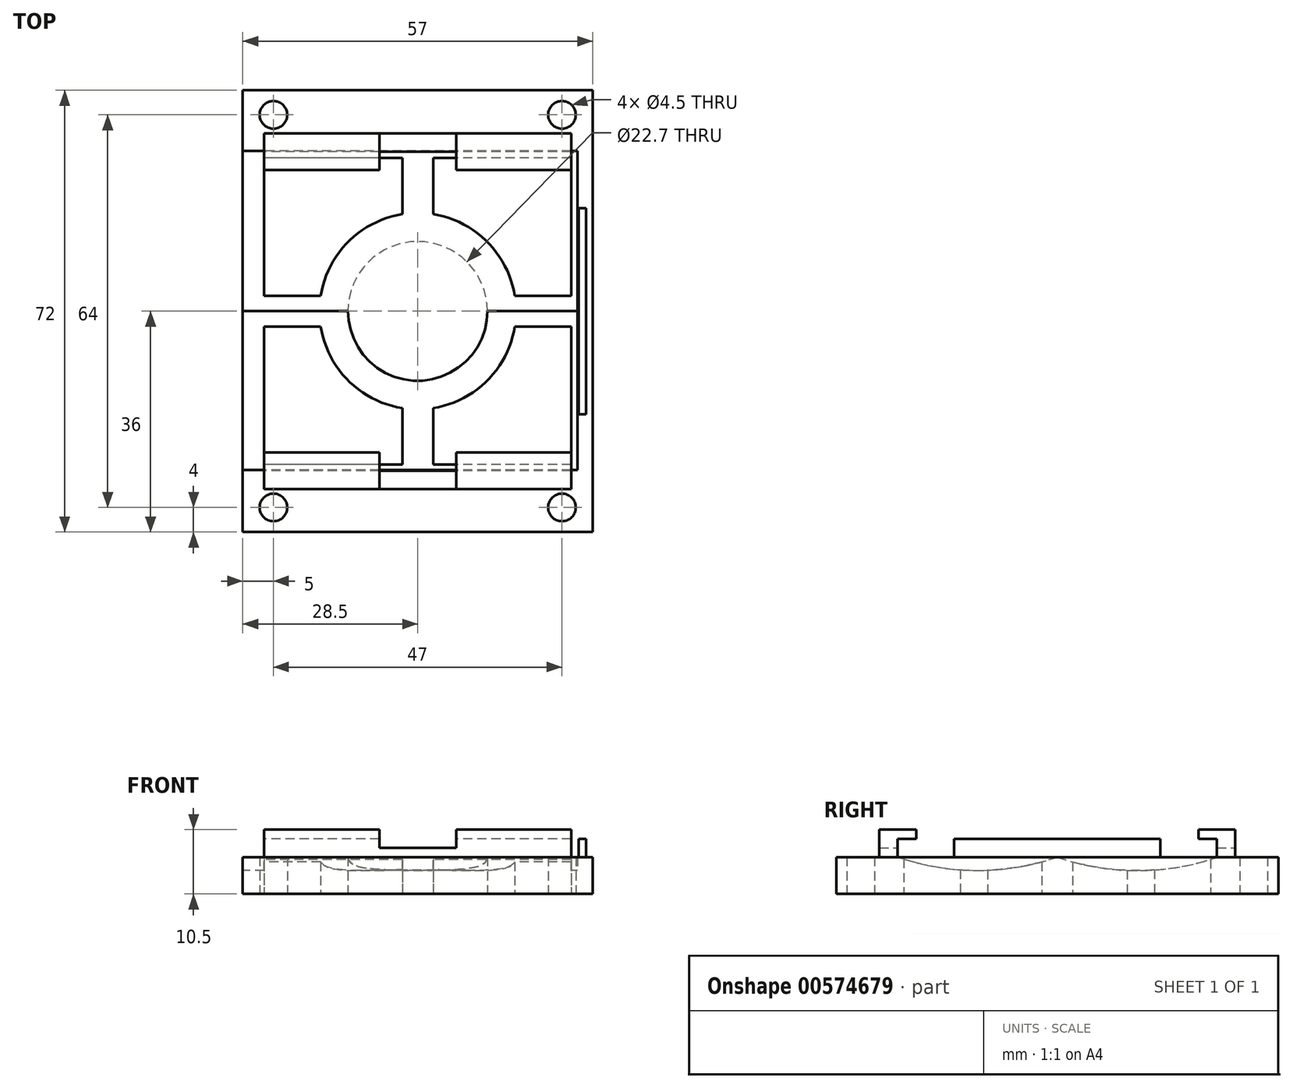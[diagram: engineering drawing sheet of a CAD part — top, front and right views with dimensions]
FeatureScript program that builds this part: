
annotation { "Feature Type Name" : "Feature", "Feature Type Description" : "" }
export const myFeature = defineFeature(function(context is Context, id is Id, definition is map)
    precondition{}
    {
        {
            var Q0;
            Q0=qCreatedBy(makeId("Top.planeOp"),FACE);
            var sketch = newSketch(context, id + "F0", { "sketchPlane" : qUnion([Q0])});
            skLineSegment(sketch, "E0.bottom", {"start": v(25, 25) * mm, "end": v(2.5, 25) * mm});
            skLineSegment(sketch, "E0.top", {"start": v(25, -25) * mm, "end": v(2.5, -25) * mm});
            skLineSegment(sketch, "E0.left", {"start": v(25, 25) * mm, "end": v(25, -25) * mm});
            skLineSegment(sketch, "E0.right", {"start": v(-25, 25) * mm, "end": v(-25, 2.5) * mm});
            skPoint(sketch, "E0.middle", {"position": v(0, 0) * mm});
            skLineSegment(sketch, "E1.bottom", {"start": v(28.5, 36) * mm, "end": v(-28.5, 36) * mm});
            skLineSegment(sketch, "E1.top", {"start": v(28.5, -36) * mm, "end": v(-28.5, -36) * mm});
            skLineSegment(sketch, "E1.left", {"start": v(28.5, 36) * mm, "end": v(28.5, -36) * mm});
            skLineSegment(sketch, "E1.right", {"start": v(-28.5, 36) * mm, "end": v(-28.5, -36) * mm});
            skCircle(sketch, "E2", {"center": v(0, 0) * mm, "radius": 11.35 * mm});
            skArc(sketch, "E3", {"start": v(2.5, -15.8) * mm, "mid": v(11.31, -11.31) * mm, "end": v(15.8, -2.5) * mm});
            skCircle(sketch, "E4", {"center": v(-23.5, 32) * mm, "radius": 2.25 * mm});
            skCircle(sketch, "E5", {"center": v(23.5, 32) * mm, "radius": 2.25 * mm});
            skCircle(sketch, "E6", {"center": v(23.5, -32) * mm, "radius": 2.25 * mm});
            skCircle(sketch, "E7", {"center": v(-23.5, -32) * mm, "radius": 2.25 * mm});
            skLineSegment(sketch, "E8.left", {"start": v(2.5, 25) * mm, "end": v(2.5, 15.8) * mm});
            skLineSegment(sketch, "E8.right", {"start": v(-2.5, 25) * mm, "end": v(-2.5, 15.8) * mm});
            skLineSegment(sketch, "E9.bottom", {"start": v(25, 2.5) * mm, "end": v(15.8, 2.5) * mm});
            skLineSegment(sketch, "E9.top", {"start": v(25, -2.5) * mm, "end": v(15.8, -2.5) * mm});
            skLineSegment(sketch, "E9.left", {"start": v(25, 2.5) * mm, "end": v(25, -2.5) * mm});
            skLineSegment(sketch, "E10.trimOffspring", {"start": v(-15.8, -2.5) * mm, "end": v(-25, -2.5) * mm});
            skLineSegment(sketch, "E11.trimOffspring", {"start": v(-2.5, -15.8) * mm, "end": v(-2.5, -25) * mm});
            skLineSegment(sketch, "E12.trimOffspring", {"start": v(2.5, -15.8) * mm, "end": v(2.5, -25) * mm});
            skLineSegment(sketch, "E13.trimOffspring", {"start": v(-15.8, 2.5) * mm, "end": v(-25, 2.5) * mm});
            skLineSegment(sketch, "E14.trimOffspring", {"start": v(-2.5, -25) * mm, "end": v(-25, -25) * mm});
            skArc(sketch, "E15.trimOffspring", {"start": v(15.8, 2.5) * mm, "mid": v(-11.31, 11.31) * mm, "end": v(-2.5, -15.8) * mm});
            skLineSegment(sketch, "E16.trimOffspring", {"start": v(-2.5, 25) * mm, "end": v(-25, 25) * mm});
            skLineSegment(sketch, "E17.trimOffspring", {"start": v(-25, -2.5) * mm, "end": v(-25, -25) * mm});
            skSolve(sketch);
        }
        {
            var Q0;
            {var subQ8=sQuery(id+"F0.wireOp",EDGE,"E0.bottom");Q0=makeQuery(id+"F0.imprint","IMPRINT",FACE,{"disambiguationData":[TD([[makeQuery(id+"F0.imprint","IMPRINT",EDGE,{"derivedFrom":subQ8}),-1.0]])]});}
            extrude(context, id + "F1", {"entities" : qUnion([Q0]), "depth" : 6 * mm, "offsetDistance" : 25 * mm});
        }
        {
            var Q0;
            Q0=makeQuery(id+"F1.opExtrude","CAP_FACE",FACE,{"disambiguationData":[OSD([sQuery(id+"F0.wireOp",EDGE,"E0.bottom"),sQuery(id+"F0.wireOp",EDGE,"E0.top"),sQuery(id+"F0.wireOp",EDGE,"E0.left"),sQuery(id+"F0.wireOp",EDGE,"E0.right"),sQuery(id+"F0.wireOp",EDGE,"E1.bottom"),sQuery(id+"F0.wireOp",EDGE,"E1.top"),sQuery(id+"F0.wireOp",EDGE,"E1.left"),sQuery(id+"F0.wireOp",EDGE,"E1.right"),sQuery(id+"F0.wireOp",EDGE,"E2"),sQuery(id+"F0.wireOp",EDGE,"E3"),sQuery(id+"F0.wireOp",EDGE,"E4"),sQuery(id+"F0.wireOp",EDGE,"E5"),sQuery(id+"F0.wireOp",EDGE,"E6"),sQuery(id+"F0.wireOp",EDGE,"E7"),sQuery(id+"F0.wireOp",EDGE,"E8.left"),sQuery(id+"F0.wireOp",EDGE,"E8.right"),sQuery(id+"F0.wireOp",EDGE,"E9.bottom"),sQuery(id+"F0.wireOp",EDGE,"E9.top"),sQuery(id+"F0.wireOp",EDGE,"E10.trimOffspring"),sQuery(id+"F0.wireOp",EDGE,"E11.trimOffspring"),sQuery(id+"F0.wireOp",EDGE,"E12.trimOffspring"),sQuery(id+"F0.wireOp",EDGE,"E13.trimOffspring"),sQuery(id+"F0.wireOp",EDGE,"E14.trimOffspring"),sQuery(id+"F0.wireOp",EDGE,"E15.trimOffspring"),sQuery(id+"F0.wireOp",EDGE,"E16.trimOffspring"),sQuery(id+"F0.wireOp",EDGE,"E17.trimOffspring")])],"isStart":false});
            var sketch = newSketch(context, id + "F2", { "sketchPlane" : qUnion([Q0])});
            skLineSegment(sketch, "E18.bottom", {"start": v(25, -26) * mm, "end": v(-25, -26) * mm});
            skLineSegment(sketch, "E18.top", {"start": v(25, 26) * mm, "end": v(-25, 26) * mm});
            skLineSegment(sketch, "E18.left", {"start": v(25, -26) * mm, "end": v(25, 26) * mm});
            skLineSegment(sketch, "E18.right", {"start": v(-25, -26) * mm, "end": v(-25, 26) * mm});
            skPoint(sketch, "E18.middle", {"position": v(0, 0) * mm});
            skLineSegment(sketch, "E19.bottom", {"start": v(25, 29) * mm, "end": v(-25, 29) * mm});
            skLineSegment(sketch, "E19.top", {"start": v(25, -29) * mm, "end": v(-25, -29) * mm});
            skLineSegment(sketch, "E19.left", {"start": v(25, 29) * mm, "end": v(25, -29) * mm});
            skLineSegment(sketch, "E19.right", {"start": v(-25, 29) * mm, "end": v(-25, -29) * mm});
            skSolve(sketch);
        }
        {
            var Q0;
            {var subQ0=sQuery(id+"F2.wireOp",EDGE,"E18.bottom");Q0=makeQuery(id+"F2.imprint","IMPRINT",FACE,{"disambiguationData":[TD([[makeQuery(id+"F2.imprint","IMPRINT",EDGE,{"derivedFrom":subQ0}),1.0]])]});}
            var Q1;
            {var subQ0=sQuery(id+"F2.wireOp",EDGE,"E18.top");Q1=makeQuery(id+"F2.imprint","IMPRINT",FACE,{"disambiguationData":[TD([[makeQuery(id+"F2.imprint","IMPRINT",EDGE,{"derivedFrom":subQ0}),-1.0]])]});}
            extrude(context, id + "F3", {"entities" : qUnion([Q0, Q1]), "operationType" : NewBodyOperationType.ADD, "depth" : 3 * mm, "offsetDistance" : 25 * mm});
        }
        {
            var Q0;
            Q0=makeQuery(id+"F3.opExtrude","CAP_FACE",FACE,{"disambiguationData":[OSD([sQuery(id+"F2.wireOp",EDGE,"E18.bottom"),sQuery(id+"F2.wireOp",EDGE,"E19.top"),sQuery(id+"F2.wireOp",EDGE,"E19.left"),sQuery(id+"F2.wireOp",EDGE,"E19.right")])],"isStart":false});
            var sketch = newSketch(context, id + "F4", { "sketchPlane" : qUnion([Q0])});
            skLineSegment(sketch, "E20.bottom", {"start": v(-25, -29) * mm, "end": v(25, -29) * mm});
            skLineSegment(sketch, "E20.top", {"start": v(-25, -23) * mm, "end": v(25, -23) * mm});
            skLineSegment(sketch, "E20.left", {"start": v(-25, -29) * mm, "end": v(-25, -23) * mm});
            skLineSegment(sketch, "E20.right", {"start": v(25, -29) * mm, "end": v(25, -23) * mm});
            skSolve(sketch);
        }
        {
            var Q0;
            {var subQ0=sQuery(id+"F4.wireOp",EDGE,"E20.top");Q0=makeQuery(id+"F4.imprint","IMPRINT",FACE,{"disambiguationData":[TD([[makeQuery(id+"F4.imprint","IMPRINT",EDGE,{"derivedFrom":subQ0}),-1.0]])]});}
            var Q1;
            {var subQ0=sQuery(id+"F4.wireOp",EDGE,"E20.bottom");Q1=makeQuery(id+"F4.imprint","IMPRINT",FACE,{"disambiguationData":[TD([[makeQuery(id+"F4.imprint","IMPRINT",EDGE,{"derivedFrom":subQ0}),-1.0]])]});}
            extrude(context, id + "F5", {"entities" : qUnion([Q0, Q1]), "operationType" : NewBodyOperationType.ADD, "depth" : 1.5 * mm, "offsetDistance" : 25 * mm});
        }
        {
            var Q0;
            Q0=makeQuery(id+"F3.opExtrude","CAP_FACE",FACE,{"disambiguationData":[OSD([sQuery(id+"F2.wireOp",EDGE,"E18.top"),sQuery(id+"F2.wireOp",EDGE,"E19.bottom"),sQuery(id+"F2.wireOp",EDGE,"E19.left"),sQuery(id+"F2.wireOp",EDGE,"E19.right")])],"isStart":false});
            var sketch = newSketch(context, id + "F6", { "sketchPlane" : qUnion([Q0])});
            skLineSegment(sketch, "E21.bottom", {"start": v(25, 29) * mm, "end": v(-25, 29) * mm});
            skLineSegment(sketch, "E21.top", {"start": v(25, 23) * mm, "end": v(-25, 23) * mm});
            skLineSegment(sketch, "E21.left", {"start": v(25, 29) * mm, "end": v(25, 23) * mm});
            skLineSegment(sketch, "E21.right", {"start": v(-25, 29) * mm, "end": v(-25, 23) * mm});
            skSolve(sketch);
        }
        {
            var Q0;
            {var subQ0=sQuery(id+"F6.wireOp",EDGE,"E21.bottom");Q0=makeQuery(id+"F6.imprint","IMPRINT",FACE,{"disambiguationData":[TD([[makeQuery(id+"F6.imprint","IMPRINT",EDGE,{"derivedFrom":subQ0}),1.0]])]});}
            var Q1;
            {var subQ0=sQuery(id+"F6.wireOp",EDGE,"E21.top");Q1=makeQuery(id+"F6.imprint","IMPRINT",FACE,{"disambiguationData":[TD([[makeQuery(id+"F6.imprint","IMPRINT",EDGE,{"derivedFrom":subQ0}),-1.0]])]});}
            extrude(context, id + "F7", {"entities" : qUnion([Q0, Q1]), "operationType" : NewBodyOperationType.ADD, "depth" : 1.5 * mm, "offsetDistance" : 25 * mm});
        }
        {
            var Q0;
            Q0=makeQuery(id+"F5.opExtrude","CAP_FACE",FACE,{"disambiguationData":[OSD([sQuery(id+"F4.wireOp",EDGE,"E20.bottom"),sQuery(id+"F4.wireOp",EDGE,"E20.top"),sQuery(id+"F4.wireOp",EDGE,"E20.left"),sQuery(id+"F4.wireOp",EDGE,"E20.right")])],"isStart":false});
            var sketch = newSketch(context, id + "F8", { "sketchPlane" : qUnion([Q0])});
            skLineSegment(sketch, "E22.bottom", {"start": v(-6.25, -33.06) * mm, "end": v(6.25, -33.06) * mm});
            skLineSegment(sketch, "E22.top", {"start": v(-6.25, 33.06) * mm, "end": v(6.25, 33.06) * mm});
            skLineSegment(sketch, "E22.left", {"start": v(-6.25, -33.06) * mm, "end": v(-6.25, 33.06) * mm});
            skLineSegment(sketch, "E22.right", {"start": v(6.25, -33.06) * mm, "end": v(6.25, 33.06) * mm});
            skPoint(sketch, "E22.middle", {"position": v(0, 0) * mm});
            skSolve(sketch);
        }
        {
            var Q0;
            Q0 = qSketchRegion(id + "F8", true);
            extrude(context, id + "F9", {"entities" : qUnion([Q0]), "operationType" : NewBodyOperationType.REMOVE, "oppositeDirection" : true, "depth" : 3 * mm, "offsetDistance" : 25 * mm});
        }
        {
            var Q0;
            Q0=makeQuery(id+"F9.boolean.opBoolean","MERGE",FACE,{"derivedFrom":[makeQuery(id+"F1.opExtrude","CAP_FACE",FACE,{"disambiguationData":[OSD([sQuery(id+"F0.wireOp",EDGE,"E0.bottom"),sQuery(id+"F0.wireOp",EDGE,"E0.top"),sQuery(id+"F0.wireOp",EDGE,"E0.left"),sQuery(id+"F0.wireOp",EDGE,"E0.right"),sQuery(id+"F0.wireOp",EDGE,"E1.bottom"),sQuery(id+"F0.wireOp",EDGE,"E1.top"),sQuery(id+"F0.wireOp",EDGE,"E1.left"),sQuery(id+"F0.wireOp",EDGE,"E1.right"),sQuery(id+"F0.wireOp",EDGE,"E2"),sQuery(id+"F0.wireOp",EDGE,"E3"),sQuery(id+"F0.wireOp",EDGE,"E4"),sQuery(id+"F0.wireOp",EDGE,"E5"),sQuery(id+"F0.wireOp",EDGE,"E6"),sQuery(id+"F0.wireOp",EDGE,"E7"),sQuery(id+"F0.wireOp",EDGE,"E8.left"),sQuery(id+"F0.wireOp",EDGE,"E8.right"),sQuery(id+"F0.wireOp",EDGE,"E9.bottom"),sQuery(id+"F0.wireOp",EDGE,"E9.top"),sQuery(id+"F0.wireOp",EDGE,"E10.trimOffspring"),sQuery(id+"F0.wireOp",EDGE,"E11.trimOffspring"),sQuery(id+"F0.wireOp",EDGE,"E12.trimOffspring"),sQuery(id+"F0.wireOp",EDGE,"E13.trimOffspring"),sQuery(id+"F0.wireOp",EDGE,"E14.trimOffspring"),sQuery(id+"F0.wireOp",EDGE,"E15.trimOffspring"),sQuery(id+"F0.wireOp",EDGE,"E16.trimOffspring"),sQuery(id+"F0.wireOp",EDGE,"E17.trimOffspring")])],"isStart":false}),makeQuery(id+"F9.opExtrude","CAP_FACE",FACE,{"disambiguationData":[OSD([sQuery(id+"F8.wireOp",EDGE,"E22.bottom"),sQuery(id+"F8.wireOp",EDGE,"E22.top"),sQuery(id+"F8.wireOp",EDGE,"E22.left"),sQuery(id+"F8.wireOp",EDGE,"E22.right")])],"isStart":false})]});
            var sketch = newSketch(context, id + "F10", { "sketchPlane" : qUnion([Q0])});
            skLineSegment(sketch, "E23.bottom", {"start": v(26.2, -16.8) * mm, "end": v(27.43, -16.8) * mm});
            skLineSegment(sketch, "E23.top", {"start": v(26.2, 16.8) * mm, "end": v(27.43, 16.8) * mm});
            skLineSegment(sketch, "E23.left", {"start": v(26.2, -16.8) * mm, "end": v(26.2, 16.8) * mm});
            skLineSegment(sketch, "E23.right", {"start": v(27.43, -16.8) * mm, "end": v(27.43, 16.8) * mm});
            skPoint(sketch, "E23.middle", {"position": v(26.81, 0) * mm});
            skSolve(sketch);
        }
        {
            var Q0;
            Q0 = qSketchRegion(id + "F10", true);
            extrude(context, id + "F11", {"entities" : qUnion([Q0]), "operationType" : NewBodyOperationType.ADD, "depth" : 3 * mm, "offsetDistance" : 25 * mm});
        }
        {
            var Q0;
            Q0=makeQuery(id+"F1.opExtrude","SWEPT_FACE",FACE,{"disambiguationData":[OSD([sQuery(id+"F0.wireOp",EDGE,"E1.right")])]});
            var sketch = newSketch(context, id + "F12", { "sketchPlane" : qUnion([Q0])});
            skArc(sketch, "E24", {"start": v(-26.09, 6) * mm, "mid": v(-13.04, 3.81) * mm, "end": v(0, 6) * mm});
            skArc(sketch, "E25", {"start": v(0, 6) * mm, "mid": v(12.96, 3.84) * mm, "end": v(25.92, 6) * mm});
            skLineSegment(sketch, "E26", {"start": v(25.92, 6) * mm, "end": v(-26.09, 6) * mm});
            skSolve(sketch);
        }
        {
            var Q0;
            {var subQ0=sQuery(id+"F12.wireOp",EDGE,"E24");Q0=makeQuery(id+"F12.imprint","IMPRINT",FACE,{"disambiguationData":[TD([[makeQuery(id+"F12.imprint","IMPRINT",EDGE,{"derivedFrom":subQ0}),1.0]])]});}
            var Q1;
            {var subQ0=sQuery(id+"F12.wireOp",EDGE,"E25");Q1=makeQuery(id+"F12.imprint","IMPRINT",FACE,{"disambiguationData":[TD([[makeQuery(id+"F12.imprint","IMPRINT",EDGE,{"derivedFrom":subQ0}),1.0]])]});}
            extrude(context, id + "F13", {"entities" : qUnion([Q0, Q1]), "operationType" : NewBodyOperationType.REMOVE, "oppositeDirection" : true, "depth" : 54.5 * mm, "offsetDistance" : 25 * mm});
        }
    });
